# Revit family: Wand- und Stielausleger- AW 30 21 FT,FT SO,A2,A4
name_source: partatom
category: Generic Models
revit_build: Autodesk Revit 2017 (Build: 20190508_0315(x64)
units: mm (PartAtom-declared; Revit-internal decimal feet)

## family parameters
Always vertical = Yes
Can host rebar = No
Cut with Voids When Loaded = No
Part Type = Normal
Room Calculation Point = No
Round Connector Dimension = Use Diameter
Shared = No
Work Plane-Based = No

## types (4) — shared parameters
Height = 69 mm
Length = 210 mm  [stored 0.688976 ft]
Manufacturer = OBO Bettermann
URL = http://www.obo-bettermann.com
Width = 50 mm  [stored 0.164042 ft]

## per-type parameters (varying)
| type | GTIN | Manufacturer Art.No. | Material 2 | Width 2 |
| AW 30 21 FT | 4012196206711 | 6419720 | Hot-dip galvanised | 19 mm |
| AW 30 21 FT SO | 4012196147496 | 7192020 | Hot-dip galvanised 85 µm | 19 mm |
| AW 30 21 A2 | 4012196209057 | 6442838 | Stainless steel, material A2 | 19 mm |
| AW 30 21 A4 | 4012196349753 | 6443311 | Stainless steel, material A4 | 20 mm |

note: column(s) folded — value = type name in every type: Article Type

note: [stored X ft] marks values corroborated as IEEE doubles in the binary element streams (Revit-internal decimal feet)

## geometry (parser evidence)
native form markers: Sweep x2
no freeform markers — native parametric forms only
